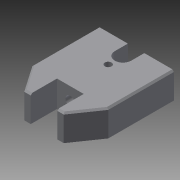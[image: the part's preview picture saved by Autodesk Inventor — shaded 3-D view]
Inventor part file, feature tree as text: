
AUTODESK INVENTOR PART (.ipt)
format: ipt  version: 2015 (Build 190159000, 159)  size: 143,360 bytes
history: native  units: in
note: dims shown in document units (in); Inventor stores cm internally (conversion verified against a paired STEP export)
features: sketch x6, extrude x4, hole x2, chamfer x1
ambient origin geometry x8: Origin, YZ Plane, XZ Plane, XY Plane, X Axis, Y Axis, Z Axis, Center Point
bodies: Solid1 (feature_tree)
feature tree (13):
  extrude  "Extrusion1"  Depth=3.5in
  extrude  "Extrusion2"  Depth=2.885in
  extrude  "Extrusion3"  Depth=0.313in
  extrude  "Extrusion4"  Depth=0.5in
  chamfer  "Chamfer1"  Distance=2.885in
  hole  "Hole1"  [1 undecoded]
  hole  "Hole2"  [1 undecoded]
  sketch  "Sketch1"  dims[d0=1.0in d1=3.5in]
  sketch  "Sketch2"  dims[d2=2.885in d3=0.0in d5=1.438in]
  sketch  "Sketch3"  dims[d6=0.313in d7=0.5in]
  sketch  "Sketch4"  dims[d8=0.0in d9=0.5in]
  sketch  "Sketch5"  dims[d10=0.5in d11=2.885in d12=0.0in]
  sketch  "Sketch6"  dims[d13=0.69in d14=0.69in d15=2.5in d16=2.5in d17=2.885in d18=0.0in d19=1.015in d20=0.938in d21=1.0in d22=0.0in d23=0.06in d24=0.125in d25=45.0deg d26=1.062in d27=1.438in d28=0.255in d29=0.75in d30=0.375in d31=0.25in d32=0.5635in d33=0.562in d34=0.8108in d35=0.5in d36=0.5075in d37=0.375in d38=0.75in d39=0.375in d40=0.25in d41=0.5635in d42=0.75in d43=0.8108in]
note: 2 required parameter values undecoded (feature->parameter linkage not recoverable at this tier; creation-order binding heuristic only, values carry confidence <= 0.55)
